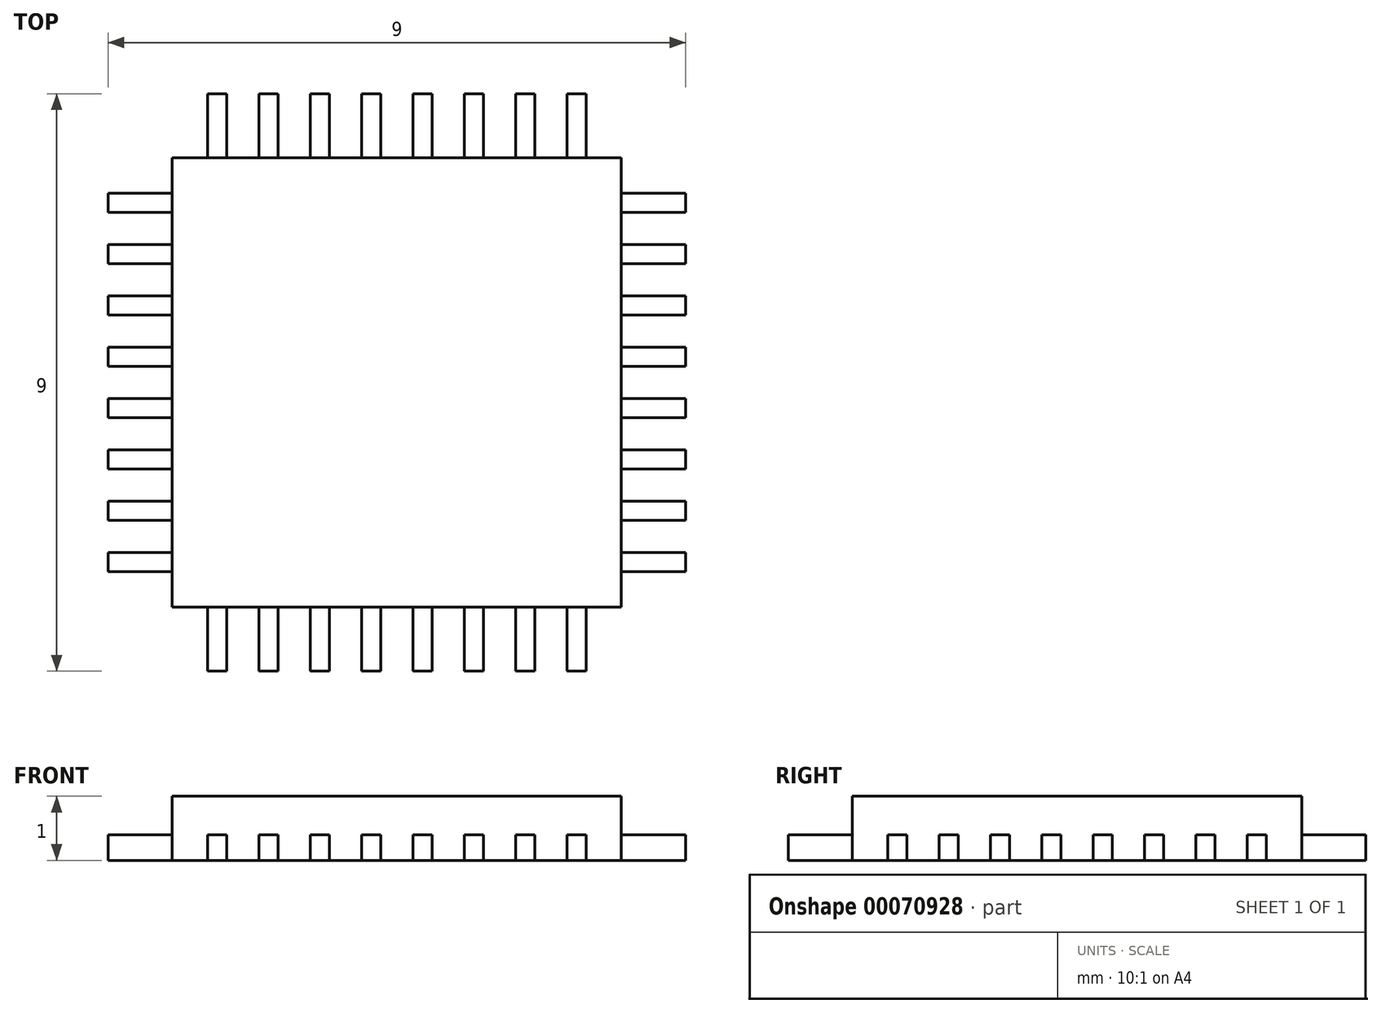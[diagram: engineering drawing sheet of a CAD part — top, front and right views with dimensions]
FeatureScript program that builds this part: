
annotation { "Feature Type Name" : "Feature", "Feature Type Description" : "" }
export const myFeature = defineFeature(function(context is Context, id is Id, definition is map)
    precondition{}
    {
        {
            var Q0;
            Q0=qCreatedBy(makeId("Top.planeOp"),FACE);
            var sketch = newSketch(context, id + "F0", { "sketchPlane" : qUnion([Q0])});
            skLineSegment(sketch, "E0.rect.bottom", {"start": v(3.5, -3.5) * mm, "end": v(-3.5, -3.5) * mm});
            skLineSegment(sketch, "E0.rect.top", {"start": v(3.5, 3.5) * mm, "end": v(-3.5, 3.5) * mm});
            skLineSegment(sketch, "E0.rect.left", {"start": v(3.5, -3.5) * mm, "end": v(3.5, 3.5) * mm});
            skLineSegment(sketch, "E0.rect.right", {"start": v(-3.5, -3.5) * mm, "end": v(-3.5, 3.5) * mm});
            skPoint(sketch, "E0.rect.middle", {"position": v(0, 0) * mm});
            skSolve(sketch);
        }
        {
            var Q0;
            Q0 = qSketchRegion(id + "F0", true);
            extrude(context, id + "F1", {"entities" : qUnion([Q0]), "depth" : 1 * mm});
        }
        {
            var Q0;
            Q0=qCreatedBy(makeId("Top.planeOp"),FACE);
            var sketch = newSketch(context, id + "F2", { "sketchPlane" : qUnion([Q0])});
            skLineSegment(sketch, "E1.bottom", {"start": v(-3.5, 2.95) * mm, "end": v(-4.5, 2.95) * mm});
            skLineSegment(sketch, "E1.top", {"start": v(-3.5, 2.65) * mm, "end": v(-4.5, 2.65) * mm});
            skLineSegment(sketch, "E1.left", {"start": v(-3.5, 2.95) * mm, "end": v(-3.5, 2.65) * mm});
            skLineSegment(sketch, "E1.right", {"start": v(-4.5, 2.95) * mm, "end": v(-4.5, 2.65) * mm});
            skLineSegment(sketch, "E2.bottom", {"start": v(-4.5, 2.15) * mm, "end": v(-3.5, 2.15) * mm});
            skLineSegment(sketch, "E2.top", {"start": v(-4.5, 1.85) * mm, "end": v(-3.5, 1.85) * mm});
            skLineSegment(sketch, "E2.left", {"start": v(-4.5, 2.15) * mm, "end": v(-4.5, 1.85) * mm});
            skLineSegment(sketch, "E2.right", {"start": v(-3.5, 2.15) * mm, "end": v(-3.5, 1.85) * mm});
            skLineSegment(sketch, "E3.bottom", {"start": v(-4.5, 1.35) * mm, "end": v(-3.5, 1.35) * mm});
            skLineSegment(sketch, "E3.top", {"start": v(-4.5, 1.05) * mm, "end": v(-3.5, 1.05) * mm});
            skLineSegment(sketch, "E3.left", {"start": v(-4.5, 1.35) * mm, "end": v(-4.5, 1.05) * mm});
            skLineSegment(sketch, "E3.right", {"start": v(-3.5, 1.35) * mm, "end": v(-3.5, 1.05) * mm});
            skLineSegment(sketch, "E4.bottom", {"start": v(-4.5, -1.05) * mm, "end": v(-3.5, -1.05) * mm});
            skLineSegment(sketch, "E4.top", {"start": v(-4.5, -1.35) * mm, "end": v(-3.5, -1.35) * mm});
            skLineSegment(sketch, "E4.left", {"start": v(-4.5, -1.05) * mm, "end": v(-4.5, -1.35) * mm});
            skLineSegment(sketch, "E4.right", {"start": v(-3.5, -1.05) * mm, "end": v(-3.5, -1.35) * mm});
            skLineSegment(sketch, "E5.bottom", {"start": v(-4.5, 0.55) * mm, "end": v(-3.5, 0.55) * mm});
            skLineSegment(sketch, "E5.top", {"start": v(-4.5, 0.25) * mm, "end": v(-3.5, 0.25) * mm});
            skLineSegment(sketch, "E5.left", {"start": v(-4.5, 0.55) * mm, "end": v(-4.5, 0.25) * mm});
            skLineSegment(sketch, "E5.right", {"start": v(-3.5, 0.55) * mm, "end": v(-3.5, 0.25) * mm});
            skLineSegment(sketch, "E6.bottom", {"start": v(-4.5, -0.25) * mm, "end": v(-3.5, -0.25) * mm});
            skLineSegment(sketch, "E6.top", {"start": v(-4.5, -0.55) * mm, "end": v(-3.5, -0.55) * mm});
            skLineSegment(sketch, "E6.left", {"start": v(-4.5, -0.25) * mm, "end": v(-4.5, -0.55) * mm});
            skLineSegment(sketch, "E6.right", {"start": v(-3.5, -0.25) * mm, "end": v(-3.5, -0.55) * mm});
            skLineSegment(sketch, "E7.bottom", {"start": v(-4.5, -1.85) * mm, "end": v(-3.5, -1.85) * mm});
            skLineSegment(sketch, "E7.top", {"start": v(-4.5, -2.15) * mm, "end": v(-3.5, -2.15) * mm});
            skLineSegment(sketch, "E7.left", {"start": v(-4.5, -1.85) * mm, "end": v(-4.5, -2.15) * mm});
            skLineSegment(sketch, "E7.right", {"start": v(-3.5, -1.85) * mm, "end": v(-3.5, -2.15) * mm});
            skLineSegment(sketch, "E8.bottom", {"start": v(-4.5, -2.65) * mm, "end": v(-3.5, -2.65) * mm});
            skLineSegment(sketch, "E8.top", {"start": v(-4.5, -2.95) * mm, "end": v(-3.5, -2.95) * mm});
            skLineSegment(sketch, "E8.left", {"start": v(-4.5, -2.65) * mm, "end": v(-4.5, -2.95) * mm});
            skLineSegment(sketch, "E8.right", {"start": v(-3.5, -2.65) * mm, "end": v(-3.5, -2.95) * mm});
            skSolve(sketch);
        }
        {
            var Q0;
            Q0 = qSketchRegion(id + "F2", true);
            extrude(context, id + "F3", {"entities" : qUnion([Q0]), "operationType" : NewBodyOperationType.ADD, "depth" : 0.4 * mm});
        }
        {
            var Q0;
            Q0=qCreatedBy(makeId("Front.planeOp"),FACE);
            var sketch = newSketch(context, id + "F4", { "sketchPlane" : qUnion([Q0])});
            skLineSegment(sketch, "E9", {"start": v(0, 0) * mm, "end": v(0, 9.6) * mm, "construction": true});
            skSolve(sketch);
        }
        {
            var Q0;
            Q0=makeQuery(id+"F1.opExtrude","SWEPT_BODY",BODY,{"disambiguationData":[OSD([sQuery(id+"F0.wireOp",EDGE,"E0.rect.bottom"),sQuery(id+"F0.wireOp",EDGE,"E0.rect.top"),sQuery(id+"F0.wireOp",EDGE,"E0.rect.left"),sQuery(id+"F0.wireOp",EDGE,"E0.rect.right")])]});
            var Q1;
            Q1=sQuery(id+"F4.wireOp",EDGE,"E9");
            circularPattern(context, id + "F5", {"operationType" : NewBodyOperationType.ADD, "entities" : qUnion([Q0]), "axis" : qUnion([Q1]), "angle" : 90 * degree, "instanceCount" : 4});
        }
    });
